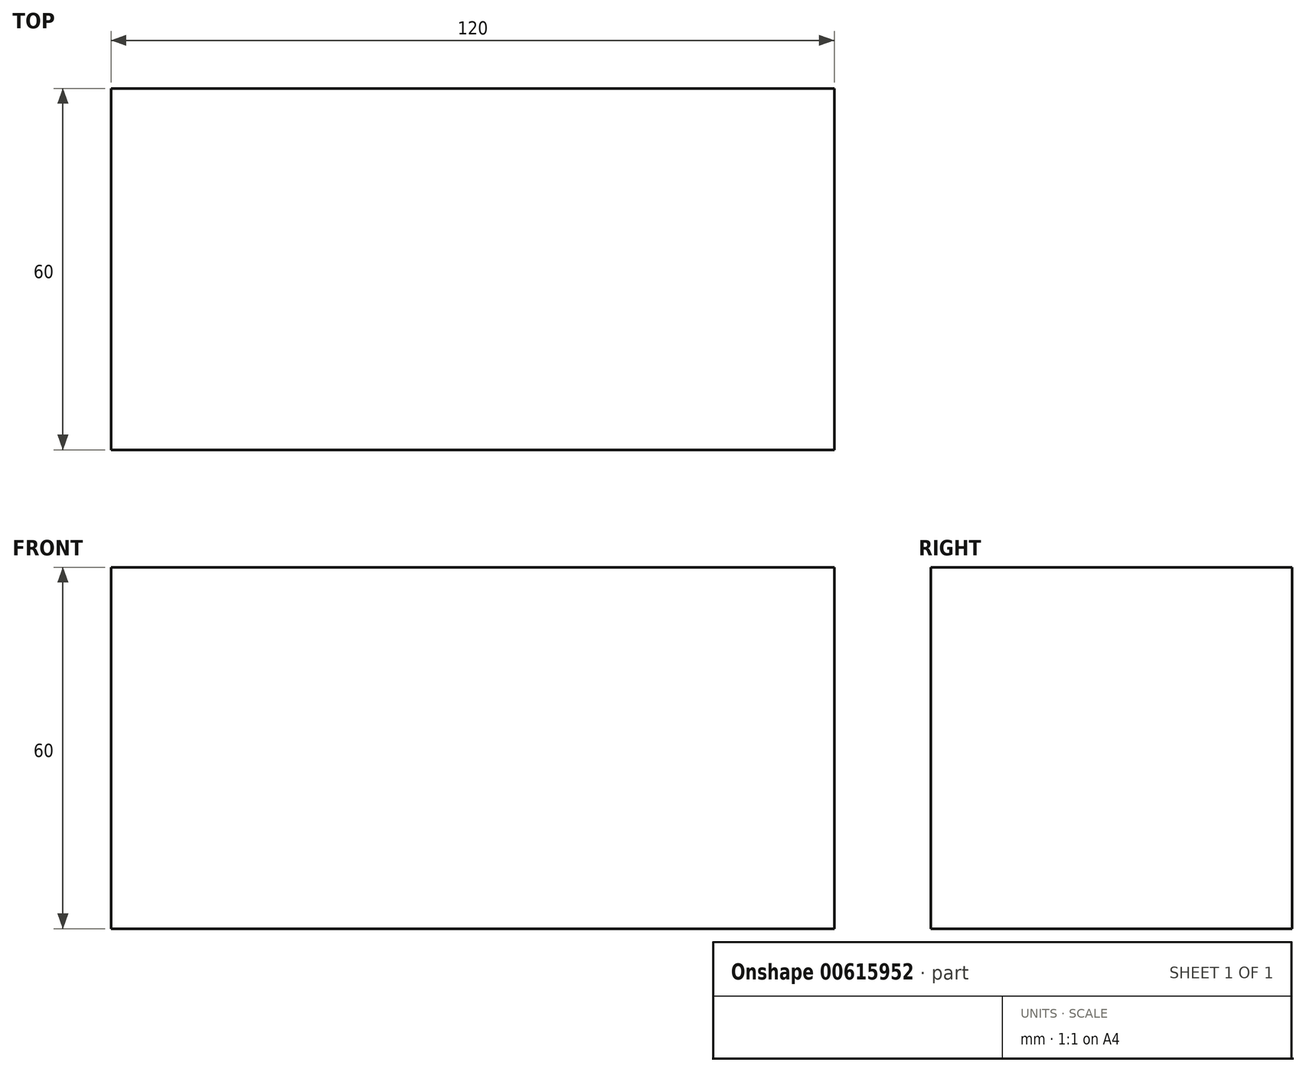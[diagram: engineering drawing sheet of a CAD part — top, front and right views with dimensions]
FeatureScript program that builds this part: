
annotation { "Feature Type Name" : "Feature", "Feature Type Description" : "" }
export const myFeature = defineFeature(function(context is Context, id is Id, definition is map)
    precondition{}
    {
        {
            var Q0;
            Q0=qCreatedBy(makeId("Front.planeOp"),FACE);
            var sketch = newSketch(context, id + "F0", { "sketchPlane" : qUnion([Q0])});
            skLineSegment(sketch, "E0", {"start": v(-75.4, 0) * mm, "end": v(44.6, 0) * mm});
            skLineSegment(sketch, "E1", {"start": v(44.6, 0) * mm, "end": v(44.6, 60) * mm});
            skLineSegment(sketch, "E2", {"start": v(44.6, 60) * mm, "end": v(-75.4, 60) * mm});
            skLineSegment(sketch, "E3", {"start": v(-75.4, 60) * mm, "end": v(-75.4, 0) * mm});
            skSolve(sketch);
        }
        {
            var Q0;
            Q0=makeQuery(id+"F0.imprint","IMPRINT",FACE,{"disambiguationData":[TD([[makeQuery(id+"F0.imprint","IMPRINT",EDGE,{"derivedFrom":sQuery(id+"F0.wireOp",EDGE,"E0")}),1.0]])]});
            extrude(context, id + "F1", {"entities" : qUnion([Q0]), "depth" : 60 * mm, "offsetDistance" : 25 * mm});
        }
    });
